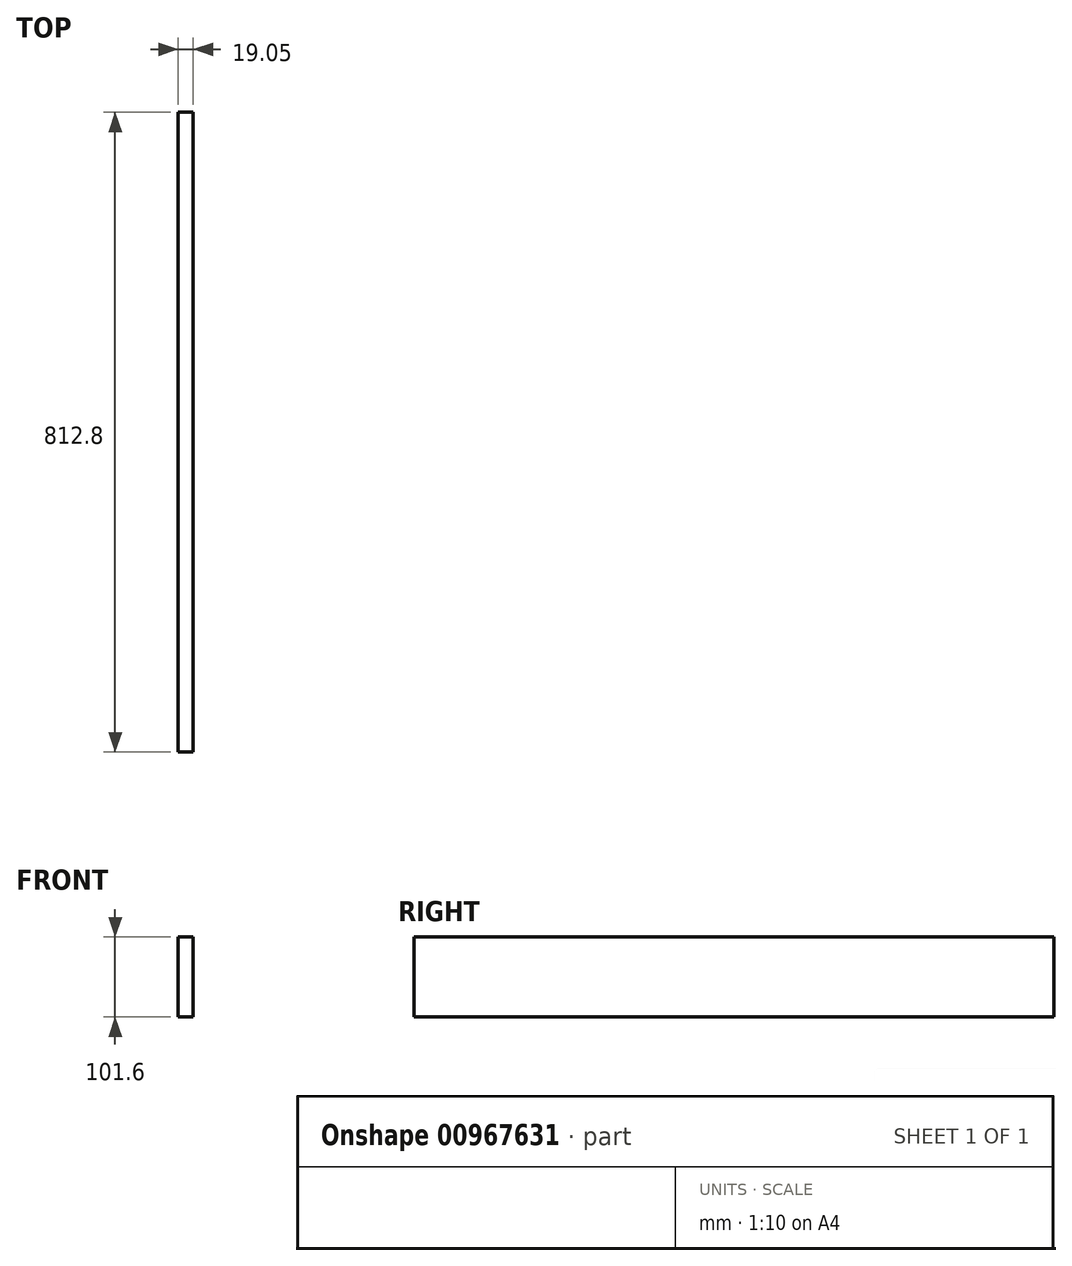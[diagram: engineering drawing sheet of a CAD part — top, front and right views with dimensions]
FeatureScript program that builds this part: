
annotation { "Feature Type Name" : "Feature", "Feature Type Description" : "" }
export const myFeature = defineFeature(function(context is Context, id is Id, definition is map)
    precondition{}
    {
        {
            var Q0;
            Q0=qCreatedBy(makeId("Right.planeOp"),FACE);
            var sketch = newSketch(context, id + "F0", { "sketchPlane" : qUnion([Q0])});
            skLineSegment(sketch, "E0.bottom", {"start": v(406.4, 50.8) * mm, "end": v(-406.4, 50.8) * mm});
            skLineSegment(sketch, "E0.top", {"start": v(406.4, -50.8) * mm, "end": v(-406.4, -50.8) * mm});
            skLineSegment(sketch, "E0.left", {"start": v(406.4, 50.8) * mm, "end": v(406.4, -50.8) * mm});
            skLineSegment(sketch, "E0.right", {"start": v(-406.4, 50.8) * mm, "end": v(-406.4, -50.8) * mm});
            skPoint(sketch, "E0.middle", {"position": v(0, 0) * mm});
            skSolve(sketch);
        }
        {
            var Q0;
            Q0 = qSketchRegion(id + "F0", true);
            extrude(context, id + "F1", {"entities" : qUnion([Q0]), "depth" : 19.05 * mm, "offsetDistance" : 25.4 * mm});
        }
    });
